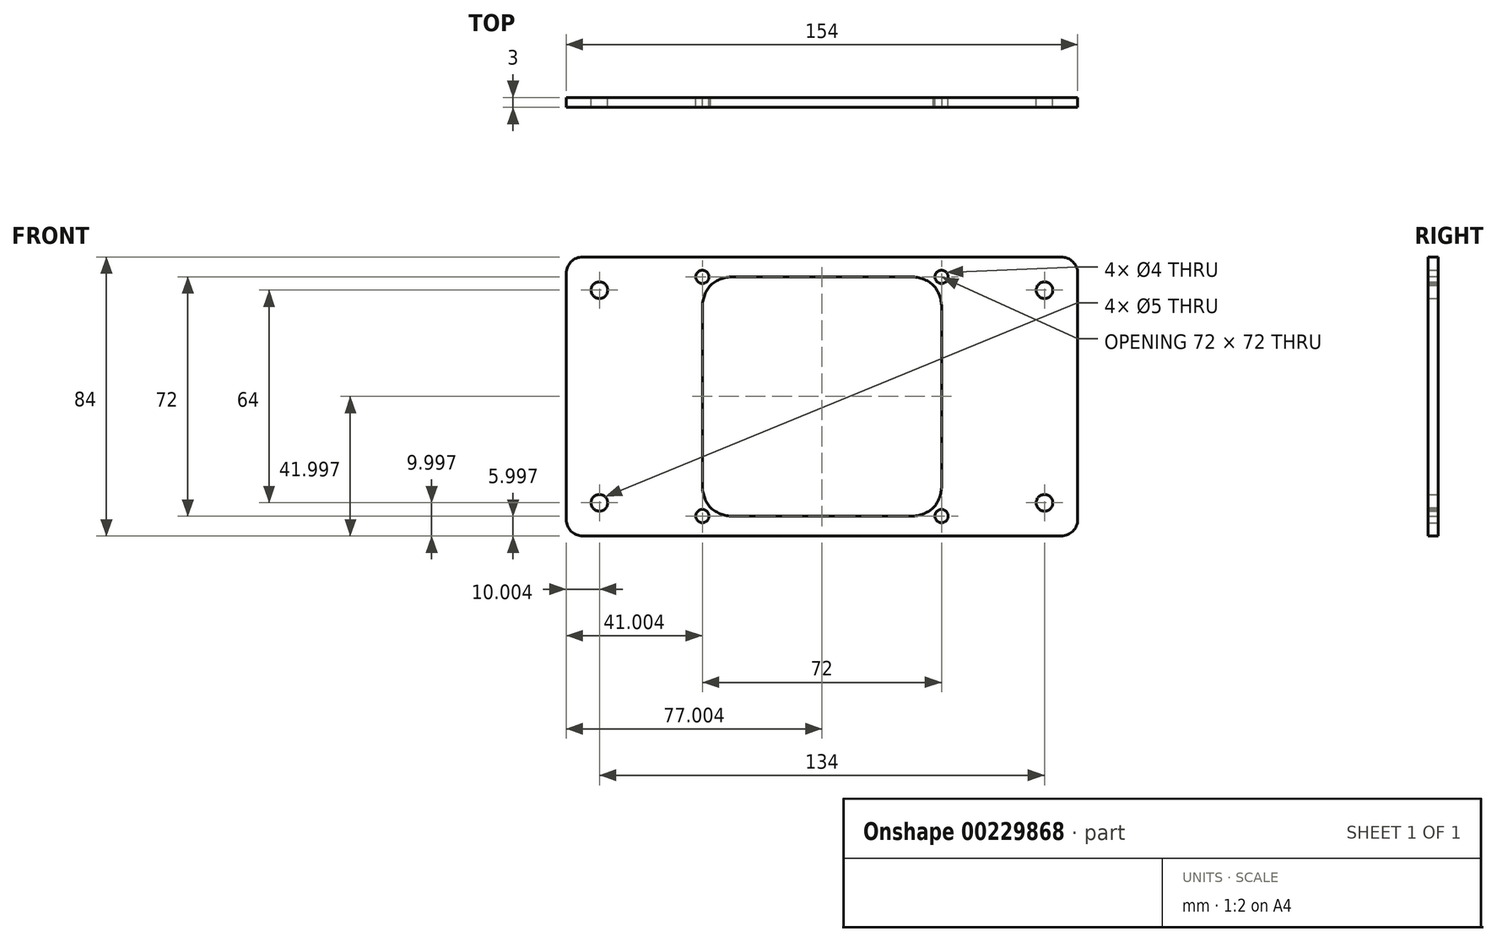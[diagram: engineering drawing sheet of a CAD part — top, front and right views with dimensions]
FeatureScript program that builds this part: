
annotation { "Feature Type Name" : "Feature", "Feature Type Description" : "" }
export const myFeature = defineFeature(function(context is Context, id is Id, definition is map)
    precondition{}
    {
        {
            var Q0;
            Q0=qCreatedBy(makeId("Front.planeOp"),FACE);
            var sketch = newSketch(context, id + "F0", { "sketchPlane" : qUnion([Q0])});
            skLineSegment(sketch, "E0.right", {"start": v(-85.76, -11.78) * mm, "end": v(-85.76, 32.22) * mm});
            skLineSegment(sketch, "E1.right", {"start": v(68.24, 2.22) * mm, "end": v(68.24, -17.78) * mm});
            skLineSegment(sketch, "E2.top", {"start": v(-80.76, 52.22) * mm, "end": v(-70.76, 52.22) * mm});
            skLineSegment(sketch, "E2.left", {"start": v(-85.76, 32.22) * mm, "end": v(-85.76, 47.22) * mm});
            skLineSegment(sketch, "E3.top", {"start": v(-80.76, -31.78) * mm, "end": v(-70.76, -31.78) * mm});
            skLineSegment(sketch, "E3.left", {"start": v(-85.76, -11.78) * mm, "end": v(-85.76, -26.78) * mm});
            skLineSegment(sketch, "E4.top", {"start": v(53.24, 52.22) * mm, "end": v(63.24, 52.22) * mm});
            skLineSegment(sketch, "E4.right", {"start": v(68.24, 32.22) * mm, "end": v(68.24, 47.22) * mm});
            skLineSegment(sketch, "E5.top", {"start": v(53.24, -31.78) * mm, "end": v(63.24, -31.78) * mm});
            skLineSegment(sketch, "E5.right", {"start": v(68.24, -11.78) * mm, "end": v(68.24, -26.78) * mm});
            skPoint(sketch, "E6.positionSnap1", {"position": v(-73.26, 52.22) * mm});
            skPoint(sketch, "E7", {"position": v(58.24, 42.22) * mm});
            skPoint(sketch, "E7.positionSnap0", {"position": v(58.24, 52.22) * mm});
            skPoint(sketch, "E7.positionSnap1", {"position": v(68.24, 42.22) * mm});
            skPoint(sketch, "E8", {"position": v(58.24, -21.78) * mm});
            skPoint(sketch, "E8.positionSnap0", {"position": v(68.24, -21.78) * mm});
            skPoint(sketch, "E8.positionSnap1", {"position": v(58.24, -31.78) * mm});
            skPoint(sketch, "E9", {"position": v(-75.76, -21.78) * mm});
            skPoint(sketch, "E9.positionSnap0", {"position": v(-85.76, -21.78) * mm});
            skPoint(sketch, "E9.positionSnap1", {"position": v(-75.76, -31.78) * mm});
            skCircle(sketch, "E10", {"center": v(58.24, 42.22) * mm, "radius": 2.5 * mm});
            skCircle(sketch, "E11", {"center": v(58.24, -21.78) * mm, "radius": 2.5 * mm});
            skCircle(sketch, "E12", {"center": v(-75.76, -21.78) * mm, "radius": 2.5 * mm});
            skPoint(sketch, "E13.visualSharp", {"position": v(48.24, 52.22) * mm});
            skPoint(sketch, "E14.visualSharp", {"position": v(68.24, 52.22) * mm});
            skArc(sketch, "E14.filletArc", {"start": v(68.24, 47.22) * mm, "mid": v(66.78, 50.75) * mm, "end": v(63.24, 52.22) * mm});
            skPoint(sketch, "E15.visualSharp", {"position": v(48.24, -31.78) * mm});
            skPoint(sketch, "E16.visualSharp", {"position": v(68.24, -31.78) * mm});
            skArc(sketch, "E16.filletArc", {"start": v(63.24, -31.78) * mm, "mid": v(66.78, -30.32) * mm, "end": v(68.24, -26.78) * mm});
            skPoint(sketch, "E17.visualSharp", {"position": v(-65.76, -31.78) * mm});
            skPoint(sketch, "E18.visualSharp", {"position": v(-85.76, -31.78) * mm});
            skArc(sketch, "E18.filletArc", {"start": v(-85.76, -26.78) * mm, "mid": v(-84.3, -30.32) * mm, "end": v(-80.76, -31.78) * mm});
            skPoint(sketch, "E19.visualSharp", {"position": v(-85.76, 52.22) * mm});
            skArc(sketch, "E19.filletArc", {"start": v(-80.76, 52.22) * mm, "mid": v(-84.3, 50.75) * mm, "end": v(-85.76, 47.22) * mm});
            skPoint(sketch, "E20.visualSharp", {"position": v(-60.76, 52.22) * mm});
            skLineSegment(sketch, "E21.left", {"start": v(-85.76, 47.22) * mm, "end": v(-85.76, 2.22) * mm});
            skLineSegment(sketch, "E22.left", {"start": v(68.24, 47.22) * mm, "end": v(68.24, -2.78) * mm});
            skLineSegment(sketch, "E23", {"start": v(-70.76, 52.22) * mm, "end": v(53.24, 52.22) * mm});
            skLineSegment(sketch, "E24", {"start": v(-70.76, -31.78) * mm, "end": v(53.24, -31.78) * mm});
            skCircle(sketch, "E25", {"center": v(-75.76, 42.22) * mm, "radius": 2.5 * mm});
            skPoint(sketch, "E26", {"position": v(-8.76, 52.22) * mm});
            skPoint(sketch, "E27", {"position": v(-8.76, 46.22) * mm});
            skPoint(sketch, "E28", {"position": v(27.24, 46.22) * mm});
            skPoint(sketch, "E29", {"position": v(-44.76, 46.22) * mm});
            skPoint(sketch, "E30", {"position": v(-44.76, -25.78) * mm});
            skPoint(sketch, "E31", {"position": v(27.24, -25.78) * mm});
            skLineSegment(sketch, "E32.bottom", {"start": v(-44.76, 46.22) * mm, "end": v(27.24, 46.22) * mm});
            skLineSegment(sketch, "E32.top", {"start": v(-44.76, -25.78) * mm, "end": v(27.24, -25.78) * mm});
            skLineSegment(sketch, "E32.left", {"start": v(-44.76, 46.22) * mm, "end": v(-44.76, -25.78) * mm});
            skLineSegment(sketch, "E32.right", {"start": v(27.24, 46.22) * mm, "end": v(27.24, -25.78) * mm});
            skCircle(sketch, "E33", {"center": v(-44.76, 46.22) * mm, "radius": 2 * mm});
            skCircle(sketch, "E34", {"center": v(27.24, 46.22) * mm, "radius": 2 * mm});
            skCircle(sketch, "E35", {"center": v(27.24, -25.78) * mm, "radius": 2 * mm});
            skCircle(sketch, "E36", {"center": v(-44.76, -25.78) * mm, "radius": 2 * mm});
            skCircle(sketch, "E37", {"center": v(-44.76, 46.22) * mm, "radius": 3.5 * mm});
            skCircle(sketch, "E38", {"center": v(-44.76, -25.78) * mm, "radius": 3.5 * mm});
            skCircle(sketch, "E39", {"center": v(27.24, -25.78) * mm, "radius": 3.5 * mm});
            skCircle(sketch, "E40", {"center": v(27.24, 46.22) * mm, "radius": 3.5 * mm});
            skSolve(sketch);
        }
        {
            var Q0;
            Q0=makeQuery(id+"F0.imprint","IMPRINT",FACE,{"disambiguationData":[TD([[makeQuery(id+"F0.imprint","IMPRINT",EDGE,{"derivedFrom":sQuery(id+"F0.wireOp",EDGE,"E0.right")}),-1.0]])]});
            var Q1;
            {var subQ0=sQuery(id+"F0.wireOp",EDGE,"E33");var subQ1=sQuery(id+"F0.wireOp",EDGE,"E32.bottom");var subQ2=makeQuery(id+"F0.imprint","INTERSECT",VERTEX,{"derivedFrom":[subQ1,subQ0]});Q1=makeQuery(id+"F0.imprint","IMPRINT",FACE,{"disambiguationData":[TD([[makeQuery(id+"F0.imprint","IMPRINT",EDGE,{"disambiguationData":[TD([[subQ2,-1.0]])],"derivedFrom":subQ1}),1.0]])]});}
            var Q2;
            {var subQ0=sQuery(id+"F0.wireOp",EDGE,"E33");var subQ1=sQuery(id+"F0.wireOp",EDGE,"E32.bottom");var subQ2=makeQuery(id+"F0.imprint","INTERSECT",VERTEX,{"derivedFrom":[subQ1,subQ0]});Q2=makeQuery(id+"F0.imprint","IMPRINT",FACE,{"disambiguationData":[TD([[makeQuery(id+"F0.imprint","IMPRINT",EDGE,{"disambiguationData":[TD([[subQ2,-1.0]])],"derivedFrom":subQ1}),-1.0]])]});}
            var Q3;
            {var subQ0=sQuery(id+"F0.wireOp",EDGE,"E36");var subQ1=sQuery(id+"F0.wireOp",EDGE,"E32.top");var subQ2=makeQuery(id+"F0.imprint","INTERSECT",VERTEX,{"derivedFrom":[subQ1,subQ0]});Q3=makeQuery(id+"F0.imprint","IMPRINT",FACE,{"disambiguationData":[TD([[makeQuery(id+"F0.imprint","IMPRINT",EDGE,{"disambiguationData":[TD([[subQ2,-1.0]])],"derivedFrom":subQ1}),-1.0]])]});}
            var Q4;
            {var subQ0=sQuery(id+"F0.wireOp",EDGE,"E36");var subQ1=sQuery(id+"F0.wireOp",EDGE,"E32.top");var subQ2=makeQuery(id+"F0.imprint","INTERSECT",VERTEX,{"derivedFrom":[subQ1,subQ0]});Q4=makeQuery(id+"F0.imprint","IMPRINT",FACE,{"disambiguationData":[TD([[makeQuery(id+"F0.imprint","IMPRINT",EDGE,{"disambiguationData":[TD([[subQ2,-1.0]])],"derivedFrom":subQ1}),1.0]])]});}
            var Q5;
            {var subQ0=sQuery(id+"F0.wireOp",EDGE,"E39");var subQ1=sQuery(id+"F0.wireOp",EDGE,"E32.top");var subQ2=makeQuery(id+"F0.imprint","INTERSECT",VERTEX,{"derivedFrom":[subQ1,subQ0]});Q5=makeQuery(id+"F0.imprint","IMPRINT",FACE,{"disambiguationData":[TD([[makeQuery(id+"F0.imprint","IMPRINT",EDGE,{"disambiguationData":[TD([[subQ2,-1.0]])],"derivedFrom":subQ1}),1.0]])]});}
            var Q6;
            {var subQ0=sQuery(id+"F0.wireOp",EDGE,"E39");var subQ1=sQuery(id+"F0.wireOp",EDGE,"E32.top");var subQ2=makeQuery(id+"F0.imprint","INTERSECT",VERTEX,{"derivedFrom":[subQ1,subQ0]});Q6=makeQuery(id+"F0.imprint","IMPRINT",FACE,{"disambiguationData":[TD([[makeQuery(id+"F0.imprint","IMPRINT",EDGE,{"disambiguationData":[TD([[subQ2,-1.0]])],"derivedFrom":subQ1}),-1.0]])]});}
            var Q7;
            {var subQ0=sQuery(id+"F0.wireOp",EDGE,"E40");var subQ1=sQuery(id+"F0.wireOp",EDGE,"E32.bottom");var subQ2=makeQuery(id+"F0.imprint","INTERSECT",VERTEX,{"derivedFrom":[subQ1,subQ0]});Q7=makeQuery(id+"F0.imprint","IMPRINT",FACE,{"disambiguationData":[TD([[makeQuery(id+"F0.imprint","IMPRINT",EDGE,{"disambiguationData":[TD([[subQ2,-1.0]])],"derivedFrom":subQ1}),-1.0]])]});}
            var Q8;
            {var subQ0=sQuery(id+"F0.wireOp",EDGE,"E40");var subQ1=sQuery(id+"F0.wireOp",EDGE,"E32.bottom");var subQ2=makeQuery(id+"F0.imprint","INTERSECT",VERTEX,{"derivedFrom":[subQ1,subQ0]});Q8=makeQuery(id+"F0.imprint","IMPRINT",FACE,{"disambiguationData":[TD([[makeQuery(id+"F0.imprint","IMPRINT",EDGE,{"disambiguationData":[TD([[subQ2,-1.0]])],"derivedFrom":subQ1}),1.0]])]});}
            extrude(context, id + "F1", {"entities" : qUnion([Q0, Q1, Q2, Q3, Q4, Q5, Q6, Q7, Q8]), "depth" : 3 * mm});
        }
        {
            var Q0;
            Q0=makeQuery(id+"F1.opExtrude","SWEPT_EDGE",EDGE,{"disambiguationData":[OSD([sQuery(id+"F0.wireOp",EDGE,"E32.right"),sQuery(id+"F0.wireOp",EDGE,"E40")])]});
            var Q1;
            Q1=makeQuery(id+"F1.opExtrude","SWEPT_EDGE",EDGE,{"disambiguationData":[OSD([sQuery(id+"F0.wireOp",EDGE,"E32.bottom"),sQuery(id+"F0.wireOp",EDGE,"E40")])]});
            var Q2;
            Q2=makeQuery(id+"F1.opExtrude","SWEPT_EDGE",EDGE,{"disambiguationData":[OSD([sQuery(id+"F0.wireOp",EDGE,"E32.bottom"),sQuery(id+"F0.wireOp",EDGE,"E37")])]});
            var Q3;
            Q3=makeQuery(id+"F1.opExtrude","SWEPT_EDGE",EDGE,{"disambiguationData":[OSD([sQuery(id+"F0.wireOp",EDGE,"E32.left"),sQuery(id+"F0.wireOp",EDGE,"E37")])]});
            var Q4;
            Q4=makeQuery(id+"F1.opExtrude","SWEPT_EDGE",EDGE,{"disambiguationData":[OSD([sQuery(id+"F0.wireOp",EDGE,"E32.left"),sQuery(id+"F0.wireOp",EDGE,"E38")])]});
            var Q5;
            Q5=makeQuery(id+"F1.opExtrude","SWEPT_EDGE",EDGE,{"disambiguationData":[OSD([sQuery(id+"F0.wireOp",EDGE,"E32.top"),sQuery(id+"F0.wireOp",EDGE,"E38")])]});
            var Q6;
            Q6=makeQuery(id+"F1.opExtrude","SWEPT_EDGE",EDGE,{"disambiguationData":[OSD([sQuery(id+"F0.wireOp",EDGE,"E32.right"),sQuery(id+"F0.wireOp",EDGE,"E39")])]});
            var Q7;
            Q7=makeQuery(id+"F1.opExtrude","SWEPT_EDGE",EDGE,{"disambiguationData":[OSD([sQuery(id+"F0.wireOp",EDGE,"E32.top"),sQuery(id+"F0.wireOp",EDGE,"E39")])]});
            fillet(context, id + "F2", {"entities" : qUnion([Q0, Q1, Q2, Q3, Q4, Q5, Q6, Q7]), "radius" : 10 * mm, "tangentPropagation" : true, "allowEdgeOverflow" : false});
        }
    });
